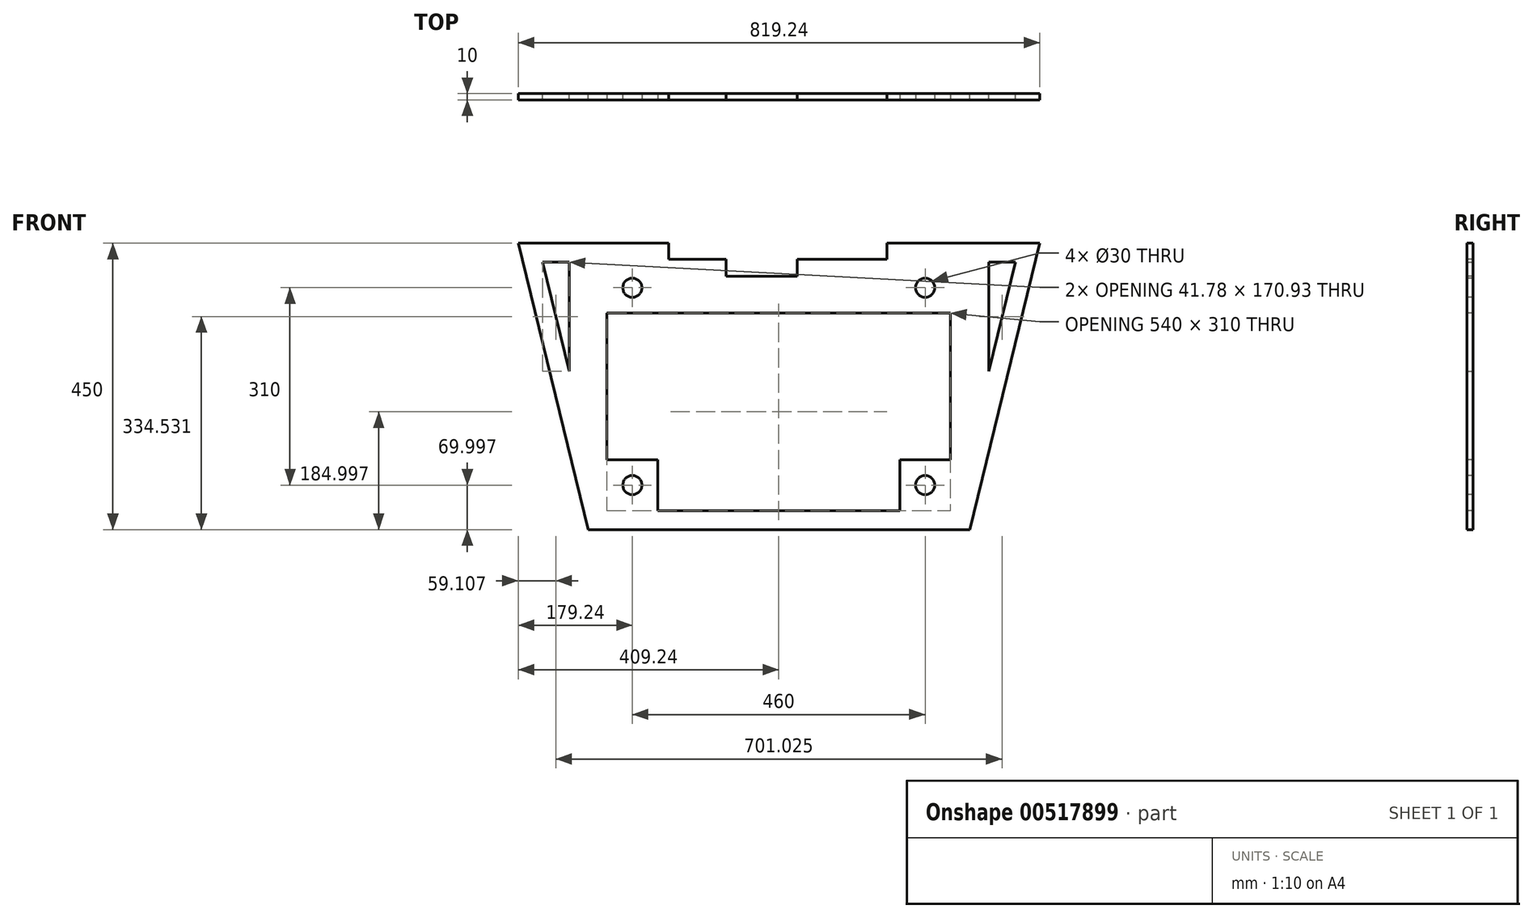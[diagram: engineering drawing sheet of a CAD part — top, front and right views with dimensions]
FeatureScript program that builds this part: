
annotation { "Feature Type Name" : "Feature", "Feature Type Description" : "" }
export const myFeature = defineFeature(function(context is Context, id is Id, definition is map)
    precondition{}
    {
        {
            var Q0;
            Q0=qCreatedBy(makeId("Front.planeOp"),FACE);
            var sketch = newSketch(context, id + "F0", { "sketchPlane" : qUnion([Q0])});
            skLineSegment(sketch, "E0.1", {"start": v(-436.34, 213.95) * mm, "end": v(-436.34, -176.05) * mm});
            skLineSegment(sketch, "E0.3", {"start": v(103.66, 213.95) * mm, "end": v(103.66, -176.05) * mm});
            skLineSegment(sketch, "E1", {"start": v(-465.58, -206.05) * mm, "end": v(133.66, -206.05) * mm});
            skLineSegment(sketch, "E2", {"start": v(-436.34, -176.05) * mm, "end": v(103.66, -176.05) * mm});
            skLineSegment(sketch, "E3", {"start": v(-436.34, 213.95) * mm, "end": v(103.66, 213.95) * mm});
            skLineSegment(sketch, "E4", {"start": v(-465.58, 243.95) * mm, "end": v(133.66, 243.95) * mm});
            skLineSegment(sketch, "E5", {"start": v(-465.58, 243.95) * mm, "end": v(-575.58, 243.95) * mm});
            skLineSegment(sketch, "E6", {"start": v(133.66, 243.95) * mm, "end": v(243.66, 243.95) * mm});
            skLineSegment(sketch, "E7", {"start": v(-575.58, 243.95) * mm, "end": v(-465.58, -206.05) * mm});
            skLineSegment(sketch, "E8", {"start": v(243.66, 243.95) * mm, "end": v(133.66, -206.05) * mm});
            skLineSegment(sketch, "E9.0", {"start": v(-537.36, 213.95) * mm, "end": v(-495.58, 43.02) * mm});
            skLineSegment(sketch, "E9.1", {"start": v(-495.58, 213.95) * mm, "end": v(-537.36, 213.95) * mm});
            skLineSegment(sketch, "E9.2", {"start": v(-495.58, 213.95) * mm, "end": v(-495.58, 43.02) * mm});
            skLineSegment(sketch, "E10.0", {"start": v(205.44, 213.95) * mm, "end": v(163.66, 43.02) * mm});
            skLineSegment(sketch, "E10.1", {"start": v(163.66, 213.95) * mm, "end": v(205.44, 213.95) * mm});
            skLineSegment(sketch, "E10.2", {"start": v(163.66, 213.95) * mm, "end": v(163.66, 43.02) * mm});
            skSolve(sketch);
        }
        {
            var Q0;
            Q0=makeQuery(id+"F0.imprint","IMPRINT",FACE,{"disambiguationData":[TD([[makeQuery(id+"F0.imprint","IMPRINT",EDGE,{"derivedFrom":sQuery(id+"F0.wireOp",EDGE,"E0.1")}),-1.0]])]});
            extrude(context, id + "F1", {"entities" : qUnion([Q0]), "depth" : 10 * mm, "offsetDistance" : 25 * mm});
        }
        {
            var Q0;
            Q0=makeQuery(id+"F1.opExtrude","CAP_FACE",FACE,{"disambiguationData":[OSD([sQuery(id+"F0.wireOp",EDGE,"E0.1"),sQuery(id+"F0.wireOp",EDGE,"E0.3"),sQuery(id+"F0.wireOp",EDGE,"E1"),sQuery(id+"F0.wireOp",EDGE,"E2"),sQuery(id+"F0.wireOp",EDGE,"E3"),sQuery(id+"F0.wireOp",EDGE,"E4"),sQuery(id+"F0.wireOp",EDGE,"E5"),sQuery(id+"F0.wireOp",EDGE,"E6"),sQuery(id+"F0.wireOp",EDGE,"E7"),sQuery(id+"F0.wireOp",EDGE,"E8"),sQuery(id+"F0.wireOp",EDGE,"E9.0"),sQuery(id+"F0.wireOp",EDGE,"E9.1"),sQuery(id+"F0.wireOp",EDGE,"E9.2"),sQuery(id+"F0.wireOp",EDGE,"E10.0"),sQuery(id+"F0.wireOp",EDGE,"E10.1"),sQuery(id+"F0.wireOp",EDGE,"E10.2")])],"isStart":false});
            var sketch = newSketch(context, id + "F2", { "sketchPlane" : qUnion([Q0])});
            skLineSegment(sketch, "E11.bottom", {"start": v(-436.34, 213.95) * mm, "end": v(-356.34, 213.95) * mm});
            skLineSegment(sketch, "E11.top", {"start": v(-436.34, 133.95) * mm, "end": v(-356.34, 133.95) * mm});
            skLineSegment(sketch, "E11.left", {"start": v(-436.34, 213.95) * mm, "end": v(-436.34, 133.95) * mm});
            skLineSegment(sketch, "E11.right", {"start": v(-356.34, 213.95) * mm, "end": v(-356.34, 133.95) * mm});
            skLineSegment(sketch, "E12.bottom", {"start": v(103.66, 213.95) * mm, "end": v(23.66, 213.95) * mm});
            skLineSegment(sketch, "E12.top", {"start": v(103.66, 133.95) * mm, "end": v(23.66, 133.95) * mm});
            skLineSegment(sketch, "E12.left", {"start": v(103.66, 213.95) * mm, "end": v(103.66, 133.95) * mm});
            skLineSegment(sketch, "E12.right", {"start": v(23.66, 213.95) * mm, "end": v(23.66, 133.95) * mm});
            skLineSegment(sketch, "E13.bottom", {"start": v(-436.34, -176.05) * mm, "end": v(-356.34, -176.05) * mm});
            skLineSegment(sketch, "E13.top", {"start": v(-436.34, -96.05) * mm, "end": v(-356.34, -96.05) * mm});
            skLineSegment(sketch, "E13.left", {"start": v(-436.34, -176.05) * mm, "end": v(-436.34, -96.05) * mm});
            skLineSegment(sketch, "E13.right", {"start": v(-356.34, -176.05) * mm, "end": v(-356.34, -96.05) * mm});
            skLineSegment(sketch, "E14.bottom", {"start": v(103.66, -176.05) * mm, "end": v(23.66, -176.05) * mm});
            skLineSegment(sketch, "E14.top", {"start": v(103.66, -96.05) * mm, "end": v(23.66, -96.05) * mm});
            skLineSegment(sketch, "E14.left", {"start": v(103.66, -176.05) * mm, "end": v(103.66, -96.05) * mm});
            skLineSegment(sketch, "E14.right", {"start": v(23.66, -176.05) * mm, "end": v(23.66, -96.05) * mm});
            skCircle(sketch, "E15", {"center": v(-396.34, -136.05) * mm, "radius": 15 * mm});
            skCircle(sketch, "E16", {"center": v(-396.34, 173.95) * mm, "radius": 15 * mm});
            skCircle(sketch, "E17", {"center": v(63.66, 173.95) * mm, "radius": 15 * mm});
            skCircle(sketch, "E18", {"center": v(63.66, -136.05) * mm, "radius": 15 * mm});
            skLineSegment(sketch, "E19", {"start": v(-356.34, 213.95) * mm, "end": v(-396.34, 243.95) * mm});
            skLineSegment(sketch, "E20", {"start": v(-356.34, 133.95) * mm, "end": v(23.66, 133.95) * mm});
            skLineSegment(sketch, "E21", {"start": v(23.66, 213.95) * mm, "end": v(63.66, 243.95) * mm});
            skLineSegment(sketch, "E22", {"start": v(-356.34, 213.95) * mm, "end": v(-249.67, 133.95) * mm});
            skLineSegment(sketch, "E23", {"start": v(23.66, 213.95) * mm, "end": v(-83, 133.95) * mm});
            skLineSegment(sketch, "E24", {"start": v(-396.34, 243.95) * mm, "end": v(63.66, 243.95) * mm});
            skSolve(sketch);
        }
        {
            var Q0;
            Q0=makeQuery(id+"F2.imprint","IMPRINT",FACE,{"disambiguationData":[TD([[makeQuery(id+"F2.imprint","IMPRINT",EDGE,{"derivedFrom":sQuery(id+"F2.wireOp",EDGE,"E11.bottom")}),-1.0]])]});
            var Q1;
            Q1=makeQuery(id+"F2.imprint","IMPRINT",FACE,{"disambiguationData":[TD([[makeQuery(id+"F2.imprint","IMPRINT",EDGE,{"derivedFrom":sQuery(id+"F2.wireOp",EDGE,"E12.bottom")}),-1.0]])]});
            var Q2;
            Q2=makeQuery(id+"F2.imprint","IMPRINT",FACE,{"disambiguationData":[TD([[makeQuery(id+"F2.imprint","IMPRINT",EDGE,{"derivedFrom":sQuery(id+"F2.wireOp",EDGE,"E14.bottom")}),1.0]])]});
            var Q3;
            Q3=makeQuery(id+"F2.imprint","IMPRINT",FACE,{"disambiguationData":[TD([[makeQuery(id+"F2.imprint","IMPRINT",EDGE,{"derivedFrom":sQuery(id+"F2.wireOp",EDGE,"E13.bottom")}),1.0]])]});
            extrude(context, id + "F3", {"entities" : qUnion([Q0, Q1, Q2, Q3]), "operationType" : NewBodyOperationType.ADD, "oppositeDirection" : true, "depth" : 10 * mm, "offsetDistance" : 25 * mm});
        }
        {
            var Q0;
            Q0=makeQuery(id+"F3.boolean.opBoolean","MERGE",FACE,{"derivedFrom":[makeQuery(id+"F1.opExtrude","CAP_FACE",FACE,{"disambiguationData":[OSD([sQuery(id+"F0.wireOp",EDGE,"E0.1"),sQuery(id+"F0.wireOp",EDGE,"E0.3"),sQuery(id+"F0.wireOp",EDGE,"E1"),sQuery(id+"F0.wireOp",EDGE,"E2"),sQuery(id+"F0.wireOp",EDGE,"E3"),sQuery(id+"F0.wireOp",EDGE,"E4"),sQuery(id+"F0.wireOp",EDGE,"E5"),sQuery(id+"F0.wireOp",EDGE,"E6"),sQuery(id+"F0.wireOp",EDGE,"E7"),sQuery(id+"F0.wireOp",EDGE,"E8"),sQuery(id+"F0.wireOp",EDGE,"E9.0"),sQuery(id+"F0.wireOp",EDGE,"E9.1"),sQuery(id+"F0.wireOp",EDGE,"E9.2"),sQuery(id+"F0.wireOp",EDGE,"E10.0"),sQuery(id+"F0.wireOp",EDGE,"E10.1"),sQuery(id+"F0.wireOp",EDGE,"E10.2")])],"isStart":false}),makeQuery(id+"F3.opExtrude","CAP_FACE",FACE,{"disambiguationData":[OSD([sQuery(id+"F2.wireOp",EDGE,"E11.bottom"),sQuery(id+"F2.wireOp",EDGE,"E11.top"),sQuery(id+"F2.wireOp",EDGE,"E11.left"),sQuery(id+"F2.wireOp",EDGE,"E11.right"),sQuery(id+"F2.wireOp",EDGE,"E16")])],"isStart":true}),makeQuery(id+"F3.opExtrude","CAP_FACE",FACE,{"disambiguationData":[OSD([sQuery(id+"F2.wireOp",EDGE,"E12.bottom"),sQuery(id+"F2.wireOp",EDGE,"E12.top"),sQuery(id+"F2.wireOp",EDGE,"E12.left"),sQuery(id+"F2.wireOp",EDGE,"E12.right"),sQuery(id+"F2.wireOp",EDGE,"E17")])],"isStart":true}),makeQuery(id+"F3.opExtrude","CAP_FACE",FACE,{"disambiguationData":[OSD([sQuery(id+"F2.wireOp",EDGE,"E13.bottom"),sQuery(id+"F2.wireOp",EDGE,"E13.top"),sQuery(id+"F2.wireOp",EDGE,"E13.left"),sQuery(id+"F2.wireOp",EDGE,"E13.right"),sQuery(id+"F2.wireOp",EDGE,"E15")])],"isStart":true}),makeQuery(id+"F3.opExtrude","CAP_FACE",FACE,{"disambiguationData":[OSD([sQuery(id+"F2.wireOp",EDGE,"E14.bottom"),sQuery(id+"F2.wireOp",EDGE,"E14.top"),sQuery(id+"F2.wireOp",EDGE,"E14.left"),sQuery(id+"F2.wireOp",EDGE,"E14.right"),sQuery(id+"F2.wireOp",EDGE,"E18")])],"isStart":true})]});
            var sketch = newSketch(context, id + "F4", { "sketchPlane" : qUnion([Q0])});
            skLineSegment(sketch, "E25", {"start": v(-356.34, 133.95) * mm, "end": v(23.66, 133.95) * mm});
            skLineSegment(sketch, "E26", {"start": v(-167.95, 292.5) * mm, "end": v(-335.9, 292.5) * mm});
            skLineSegment(sketch, "E27", {"start": v(-167.95, 292.5) * mm, "end": v(0, 292.5) * mm});
            skPoint(sketch, "E28.start.orphan", {"position": v(-166.34, 213.95) * mm});
            skLineSegment(sketch, "E29", {"start": v(-356.34, 243.95) * mm, "end": v(23.66, 243.95) * mm});
            skLineSegment(sketch, "E30", {"start": v(-286.97, 218.5) * mm, "end": v(3.6, 218.5) * mm});
            skLineSegment(sketch, "E31", {"start": v(-286.97, 218.5) * mm, "end": v(-339, 218.5) * mm});
            skPoint(sketch, "E32.orphan", {"position": v(-335.9, 213.95) * mm});
            skPoint(sketch, "E33.orphan", {"position": v(0, 213.95) * mm});
            skLineSegment(sketch, "E34", {"start": v(-339, 218.5) * mm, "end": v(-339, 243.95) * mm});
            skLineSegment(sketch, "E35", {"start": v(3.6, 218.5) * mm, "end": v(3.6, 243.95) * mm});
            skSolve(sketch);
        }
        {
            var Q0;
            Q0=makeQuery(id+"F3.boolean.opBoolean","MERGE",FACE,{"derivedFrom":[makeQuery(id+"F1.opExtrude","CAP_FACE",FACE,{"disambiguationData":[OSD([sQuery(id+"F0.wireOp",EDGE,"E0.1"),sQuery(id+"F0.wireOp",EDGE,"E0.3"),sQuery(id+"F0.wireOp",EDGE,"E1"),sQuery(id+"F0.wireOp",EDGE,"E2"),sQuery(id+"F0.wireOp",EDGE,"E3"),sQuery(id+"F0.wireOp",EDGE,"E4"),sQuery(id+"F0.wireOp",EDGE,"E5"),sQuery(id+"F0.wireOp",EDGE,"E6"),sQuery(id+"F0.wireOp",EDGE,"E7"),sQuery(id+"F0.wireOp",EDGE,"E8"),sQuery(id+"F0.wireOp",EDGE,"E9.0"),sQuery(id+"F0.wireOp",EDGE,"E9.1"),sQuery(id+"F0.wireOp",EDGE,"E9.2"),sQuery(id+"F0.wireOp",EDGE,"E10.0"),sQuery(id+"F0.wireOp",EDGE,"E10.1"),sQuery(id+"F0.wireOp",EDGE,"E10.2")])],"isStart":false}),makeQuery(id+"F3.opExtrude","CAP_FACE",FACE,{"disambiguationData":[OSD([sQuery(id+"F2.wireOp",EDGE,"E11.bottom"),sQuery(id+"F2.wireOp",EDGE,"E11.top"),sQuery(id+"F2.wireOp",EDGE,"E11.left"),sQuery(id+"F2.wireOp",EDGE,"E11.right"),sQuery(id+"F2.wireOp",EDGE,"E16")])],"isStart":true}),makeQuery(id+"F3.opExtrude","CAP_FACE",FACE,{"disambiguationData":[OSD([sQuery(id+"F2.wireOp",EDGE,"E12.bottom"),sQuery(id+"F2.wireOp",EDGE,"E12.top"),sQuery(id+"F2.wireOp",EDGE,"E12.left"),sQuery(id+"F2.wireOp",EDGE,"E12.right"),sQuery(id+"F2.wireOp",EDGE,"E17")])],"isStart":true}),makeQuery(id+"F3.opExtrude","CAP_FACE",FACE,{"disambiguationData":[OSD([sQuery(id+"F2.wireOp",EDGE,"E13.bottom"),sQuery(id+"F2.wireOp",EDGE,"E13.top"),sQuery(id+"F2.wireOp",EDGE,"E13.left"),sQuery(id+"F2.wireOp",EDGE,"E13.right"),sQuery(id+"F2.wireOp",EDGE,"E15")])],"isStart":true}),makeQuery(id+"F3.opExtrude","CAP_FACE",FACE,{"disambiguationData":[OSD([sQuery(id+"F2.wireOp",EDGE,"E14.bottom"),sQuery(id+"F2.wireOp",EDGE,"E14.top"),sQuery(id+"F2.wireOp",EDGE,"E14.left"),sQuery(id+"F2.wireOp",EDGE,"E14.right"),sQuery(id+"F2.wireOp",EDGE,"E18")])],"isStart":true})]});
            var sketch = newSketch(context, id + "F5", { "sketchPlane" : qUnion([Q0])});
            skLineSegment(sketch, "E36.bottom", {"start": v(-356.34, 213.95) * mm, "end": v(23.66, 213.95) * mm});
            skLineSegment(sketch, "E36.top", {"start": v(-356.34, 133.95) * mm, "end": v(23.66, 133.95) * mm});
            skLineSegment(sketch, "E36.left", {"start": v(-356.34, 213.95) * mm, "end": v(-356.34, 133.95) * mm});
            skLineSegment(sketch, "E36.right", {"start": v(23.66, 213.95) * mm, "end": v(23.66, 133.95) * mm});
            skSolve(sketch);
        }
        {
            var Q0;
            Q0=makeQuery(id+"F5.imprint","IMPRINT",FACE,{"disambiguationData":[TD([[makeQuery(id+"F5.imprint","IMPRINT",EDGE,{"derivedFrom":sQuery(id+"F5.wireOp",EDGE,"E36.bottom")}),-1.0]])]});
            extrude(context, id + "F6", {"entities" : qUnion([Q0]), "operationType" : NewBodyOperationType.ADD, "oppositeDirection" : true, "depth" : 10 * mm, "offsetDistance" : 25 * mm});
        }
        {
            var Q0;
            Q0=makeQuery(id+"F4.imprint","IMPRINT",FACE,{"disambiguationData":[TD([[makeQuery(id+"F4.imprint","IMPRINT",EDGE,{"derivedFrom":sQuery(id+"F4.wireOp",EDGE,"E30")}),1.0]])]});
            extrude(context, id + "F7", {"entities" : qUnion([Q0]), "operationType" : NewBodyOperationType.REMOVE, "oppositeDirection" : true, "depth" : 25 * mm, "offsetDistance" : 25 * mm});
        }
        {
            var Q0;
            Q0=makeQuery(id+"F6.boolean.opBoolean","MERGE",FACE,{"derivedFrom":[makeQuery(id+"F3.boolean.opBoolean","MERGE",FACE,{"derivedFrom":[makeQuery(id+"F1.opExtrude","CAP_FACE",FACE,{"disambiguationData":[OSD([sQuery(id+"F0.wireOp",EDGE,"E0.1"),sQuery(id+"F0.wireOp",EDGE,"E0.3"),sQuery(id+"F0.wireOp",EDGE,"E1"),sQuery(id+"F0.wireOp",EDGE,"E2"),sQuery(id+"F0.wireOp",EDGE,"E3"),sQuery(id+"F0.wireOp",EDGE,"E4"),sQuery(id+"F0.wireOp",EDGE,"E5"),sQuery(id+"F0.wireOp",EDGE,"E6"),sQuery(id+"F0.wireOp",EDGE,"E7"),sQuery(id+"F0.wireOp",EDGE,"E8"),sQuery(id+"F0.wireOp",EDGE,"E9.0"),sQuery(id+"F0.wireOp",EDGE,"E9.1"),sQuery(id+"F0.wireOp",EDGE,"E9.2"),sQuery(id+"F0.wireOp",EDGE,"E10.0"),sQuery(id+"F0.wireOp",EDGE,"E10.1"),sQuery(id+"F0.wireOp",EDGE,"E10.2")])],"isStart":false}),makeQuery(id+"F3.opExtrude","CAP_FACE",FACE,{"disambiguationData":[OSD([sQuery(id+"F2.wireOp",EDGE,"E11.bottom"),sQuery(id+"F2.wireOp",EDGE,"E11.top"),sQuery(id+"F2.wireOp",EDGE,"E11.left"),sQuery(id+"F2.wireOp",EDGE,"E11.right"),sQuery(id+"F2.wireOp",EDGE,"E16")])],"isStart":true}),makeQuery(id+"F3.opExtrude","CAP_FACE",FACE,{"disambiguationData":[OSD([sQuery(id+"F2.wireOp",EDGE,"E12.bottom"),sQuery(id+"F2.wireOp",EDGE,"E12.top"),sQuery(id+"F2.wireOp",EDGE,"E12.left"),sQuery(id+"F2.wireOp",EDGE,"E12.right"),sQuery(id+"F2.wireOp",EDGE,"E17")])],"isStart":true}),makeQuery(id+"F3.opExtrude","CAP_FACE",FACE,{"disambiguationData":[OSD([sQuery(id+"F2.wireOp",EDGE,"E13.bottom"),sQuery(id+"F2.wireOp",EDGE,"E13.top"),sQuery(id+"F2.wireOp",EDGE,"E13.left"),sQuery(id+"F2.wireOp",EDGE,"E13.right"),sQuery(id+"F2.wireOp",EDGE,"E15")])],"isStart":true}),makeQuery(id+"F3.opExtrude","CAP_FACE",FACE,{"disambiguationData":[OSD([sQuery(id+"F2.wireOp",EDGE,"E14.bottom"),sQuery(id+"F2.wireOp",EDGE,"E14.top"),sQuery(id+"F2.wireOp",EDGE,"E14.left"),sQuery(id+"F2.wireOp",EDGE,"E14.right"),sQuery(id+"F2.wireOp",EDGE,"E18")])],"isStart":true})]}),makeQuery(id+"F6.opExtrude","CAP_FACE",FACE,{"disambiguationData":[OSD([sQuery(id+"F5.wireOp",EDGE,"E36.bottom"),sQuery(id+"F5.wireOp",EDGE,"E36.top"),sQuery(id+"F5.wireOp",EDGE,"E36.left"),sQuery(id+"F5.wireOp",EDGE,"E36.right")])],"isStart":true})]});
            var sketch = newSketch(context, id + "F8", { "sketchPlane" : qUnion([Q0])});
            skLineSegment(sketch, "E37", {"start": v(-248.92, 218.6) * mm, "end": v(-248.92, 192.27) * mm});
            skLineSegment(sketch, "E38", {"start": v(-248.92, 192.27) * mm, "end": v(-137.15, 192.27) * mm});
            skLineSegment(sketch, "E39", {"start": v(-137.15, 192.27) * mm, "end": v(-137.15, 218.6) * mm});
            skLineSegment(sketch, "E40", {"start": v(-339, 218.5) * mm, "end": v(-249, 218.5) * mm});
            skLineSegment(sketch, "E41", {"start": v(-248.92, 218.6) * mm, "end": v(-137.15, 218.6) * mm});
            skSolve(sketch);
        }
        {
            var Q0;
            {var subQ0=sQuery(id+"F8.wireOp",EDGE,"E38");Q0=makeQuery(id+"F8.imprint","IMPRINT",FACE,{"disambiguationData":[TD([[makeQuery(id+"F8.imprint","IMPRINT",EDGE,{"derivedFrom":subQ0}),1.0]])]});}
            extrude(context, id + "F9", {"entities" : qUnion([Q0]), "operationType" : NewBodyOperationType.REMOVE, "oppositeDirection" : true, "depth" : 25 * mm, "offsetDistance" : 25 * mm});
        }
    });
